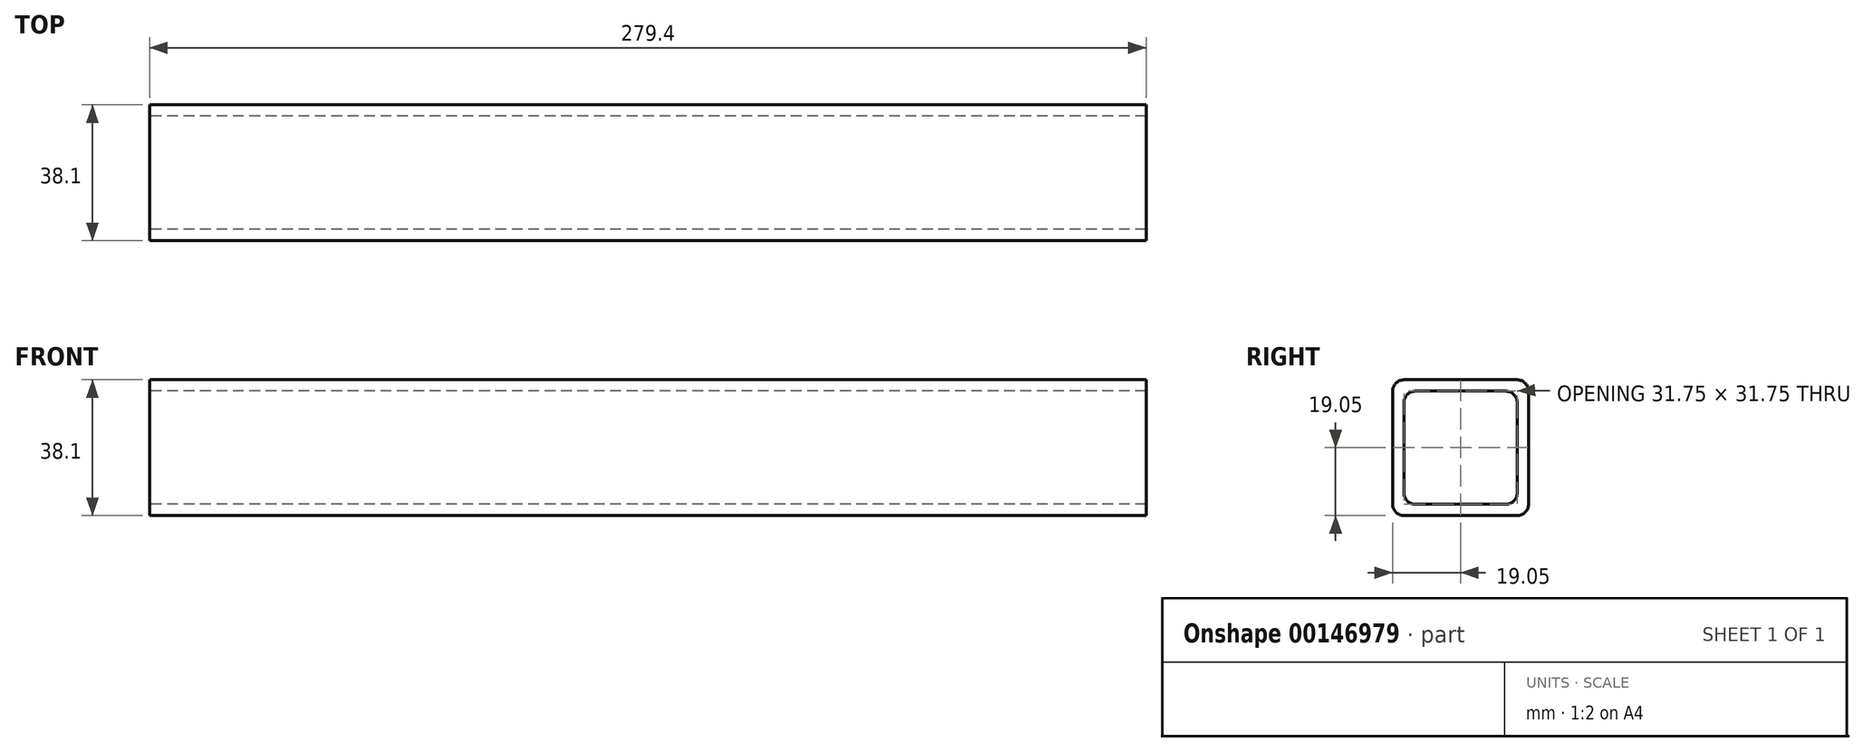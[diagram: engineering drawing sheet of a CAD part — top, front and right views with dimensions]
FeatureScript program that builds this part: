
annotation { "Feature Type Name" : "Feature", "Feature Type Description" : "" }
export const myFeature = defineFeature(function(context is Context, id is Id, definition is map)
    precondition{}
    {
        {
            var Q0;
            Q0=qCreatedBy(makeId("Right.planeOp"),FACE);
            var sketch = newSketch(context, id + "F0", { "sketchPlane" : qUnion([Q0])});
            skLineSegment(sketch, "E0.bottom", {"start": v(15.87, 19.05) * mm, "end": v(-15.88, 19.05) * mm});
            skLineSegment(sketch, "E0.top", {"start": v(15.88, -19.05) * mm, "end": v(-15.87, -19.05) * mm});
            skLineSegment(sketch, "E0.left", {"start": v(19.05, 15.88) * mm, "end": v(19.05, -15.88) * mm});
            skLineSegment(sketch, "E0.right", {"start": v(-19.05, 15.87) * mm, "end": v(-19.05, -15.88) * mm});
            skPoint(sketch, "E0.middle", {"position": v(0, 0) * mm});
            skPoint(sketch, "E1.visualSharp", {"position": v(-19.05, 19.05) * mm});
            skArc(sketch, "E1.filletArc", {"start": v(-15.88, 19.05) * mm, "mid": v(-18.12, 18.12) * mm, "end": v(-19.05, 15.87) * mm});
            skPoint(sketch, "E2.visualSharp", {"position": v(19.05, 19.05) * mm});
            skArc(sketch, "E2.filletArc", {"start": v(19.05, 15.88) * mm, "mid": v(18.12, 18.12) * mm, "end": v(15.87, 19.05) * mm});
            skPoint(sketch, "E3.visualSharp", {"position": v(-19.05, -19.05) * mm});
            skArc(sketch, "E3.filletArc", {"start": v(-19.05, -15.88) * mm, "mid": v(-18.12, -18.12) * mm, "end": v(-15.87, -19.05) * mm});
            skPoint(sketch, "E4.visualSharp", {"position": v(19.05, -19.05) * mm});
            skArc(sketch, "E4.filletArc", {"start": v(15.88, -19.05) * mm, "mid": v(18.12, -18.12) * mm, "end": v(19.05, -15.88) * mm});
            skLineSegment(sketch, "E5.bottom", {"start": v(12.7, 15.88) * mm, "end": v(-12.7, 15.88) * mm});
            skLineSegment(sketch, "E5.top", {"start": v(12.7, -15.88) * mm, "end": v(-12.7, -15.88) * mm});
            skLineSegment(sketch, "E5.left", {"start": v(15.88, 12.7) * mm, "end": v(15.88, -12.7) * mm});
            skLineSegment(sketch, "E5.right", {"start": v(-15.88, 12.7) * mm, "end": v(-15.88, -12.7) * mm});
            skArc(sketch, "E6.filletArc", {"start": v(-12.7, 15.88) * mm, "mid": v(-14.95, 14.95) * mm, "end": v(-15.88, 12.7) * mm});
            skPoint(sketch, "E7.visualSharp", {"position": v(15.88, 15.88) * mm});
            skArc(sketch, "E7.filletArc", {"start": v(15.88, 12.7) * mm, "mid": v(14.95, 14.95) * mm, "end": v(12.7, 15.88) * mm});
            skPoint(sketch, "E8.visualSharp", {"position": v(-15.88, -15.88) * mm});
            skArc(sketch, "E8.filletArc", {"start": v(-15.88, -12.7) * mm, "mid": v(-14.95, -14.95) * mm, "end": v(-12.7, -15.88) * mm});
            skPoint(sketch, "E9.visualSharp", {"position": v(15.88, -15.87) * mm});
            skArc(sketch, "E9.filletArc", {"start": v(12.7, -15.88) * mm, "mid": v(14.95, -14.95) * mm, "end": v(15.88, -12.7) * mm});
            skSolve(sketch);
        }
        {
            var Q0;
            Q0 = qSketchRegion(id + "F0", true);
            extrude(context, id + "F1", {"entities" : qUnion([Q0]), "depth" : 279.4 * mm});
        }
    });
